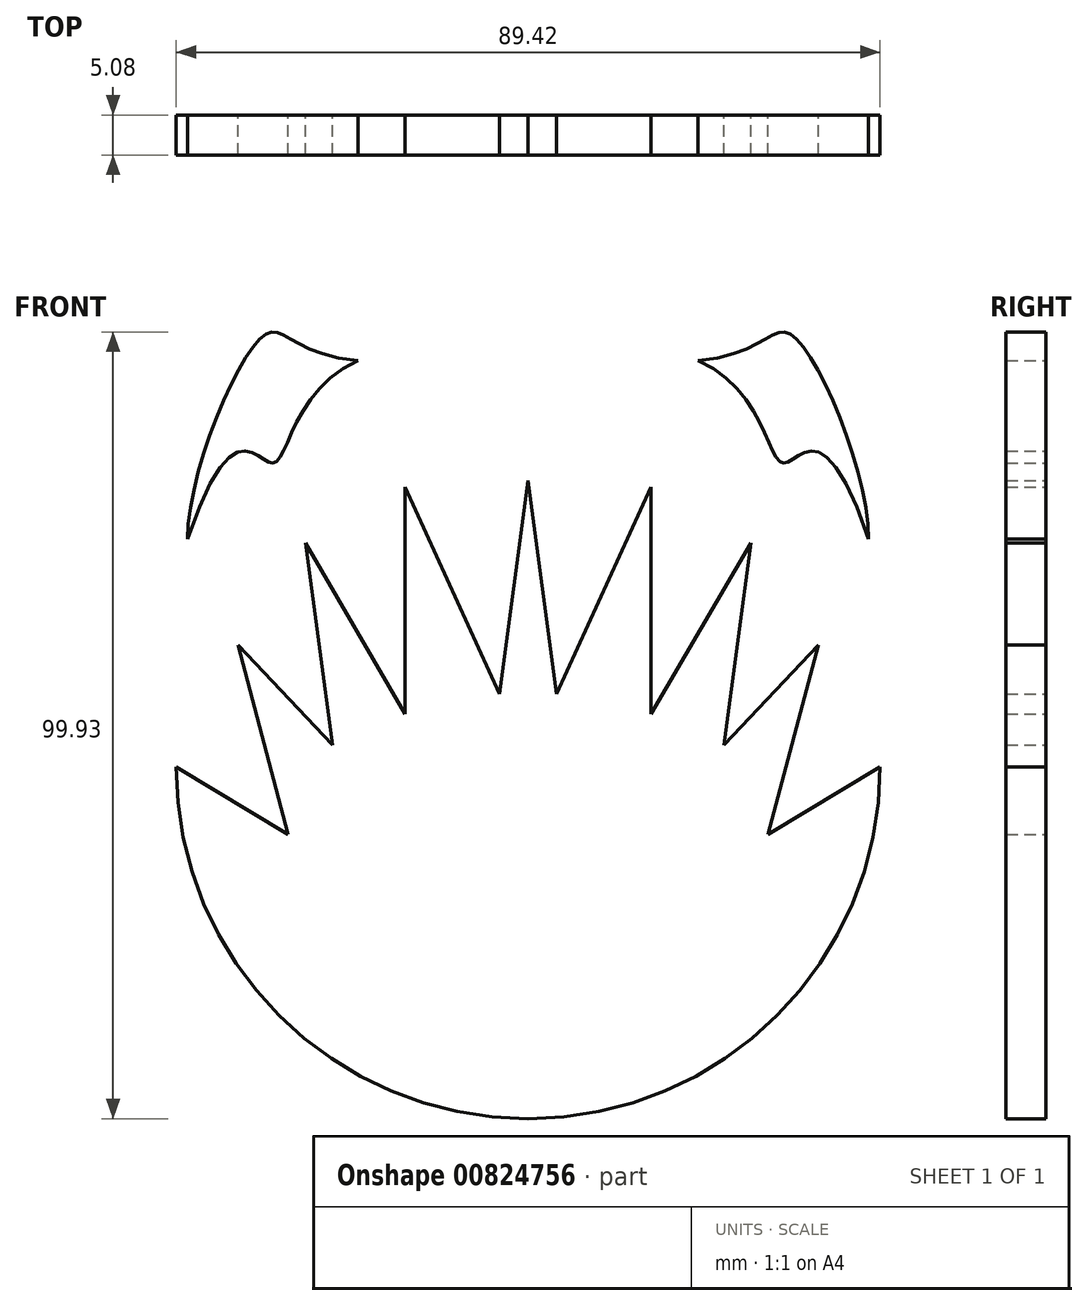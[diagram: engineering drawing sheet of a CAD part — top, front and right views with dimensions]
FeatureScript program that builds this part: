
annotation { "Feature Type Name" : "Feature", "Feature Type Description" : "" }
export const myFeature = defineFeature(function(context is Context, id is Id, definition is map)
    precondition{}
    {
        {
            var Q0;
            Q0=qCreatedBy(makeId("Front.planeOp"),FACE);
            var sketch = newSketch(context, id + "F0", { "sketchPlane" : qUnion([Q0])});
            skArc(sketch, "E0", {"start": v(-44.71, 0) * mm, "mid": v(0, -44.71) * mm, "end": v(44.71, 0) * mm});
            skLineSegment(sketch, "E1", {"start": v(0, 36.33) * mm, "end": v(3.6, 9.24) * mm});
            skLineSegment(sketch, "E2", {"start": v(3.6, 9.24) * mm, "end": v(15.63, 35.53) * mm});
            skLineSegment(sketch, "E3", {"start": v(15.63, 35.53) * mm, "end": v(15.63, 6.69) * mm});
            skLineSegment(sketch, "E4", {"start": v(15.63, 6.69) * mm, "end": v(28.3, 28.4) * mm});
            skLineSegment(sketch, "E5", {"start": v(28.3, 28.4) * mm, "end": v(24.87, 2.77) * mm});
            skLineSegment(sketch, "E6", {"start": v(24.87, 2.77) * mm, "end": v(36.87, 15.46) * mm});
            skLineSegment(sketch, "E7", {"start": v(36.87, 15.46) * mm, "end": v(30.5, -8.6) * mm});
            skLineSegment(sketch, "E8", {"start": v(30.5, -8.6) * mm, "end": v(44.71, 0) * mm});
            skLineSegment(sketch, "E9.MirrorCS", {"start": v(0, 36.33) * mm, "end": v(-3.6, 9.24) * mm});
            skLineSegment(sketch, "E10.MirrorCS", {"start": v(-3.6, 9.24) * mm, "end": v(-15.63, 35.53) * mm});
            skLineSegment(sketch, "E11.MirrorCS", {"start": v(-15.63, 35.53) * mm, "end": v(-15.63, 6.69) * mm});
            skLineSegment(sketch, "E12.MirrorCS", {"start": v(-15.63, 6.69) * mm, "end": v(-28.3, 28.4) * mm});
            skLineSegment(sketch, "E13.MirrorCS", {"start": v(-28.3, 28.4) * mm, "end": v(-24.87, 2.77) * mm});
            skLineSegment(sketch, "E14.MirrorCS", {"start": v(-24.87, 2.77) * mm, "end": v(-36.87, 15.46) * mm});
            skLineSegment(sketch, "E15.MirrorCS", {"start": v(-36.87, 15.46) * mm, "end": v(-30.5, -8.6) * mm});
            skLineSegment(sketch, "E16.MirrorCS", {"start": v(-30.5, -8.6) * mm, "end": v(-44.71, 0) * mm});
            skFitSpline(sketch, "E17", {"points": [v(-43.26, 28.91) * mm, v(-33.44, 54.85) * mm, v(-21.59, 51.57) * mm], "startDerivative": vector(0, 41.8) * mm, "endDerivative": vector(62.53, -5.77) * mm});
            skFitSpline(sketch, "E18", {"points": [v(-43.26, 28.91) * mm, v(-32.42, 38.58) * mm, v(-21.59, 51.57) * mm], "startDerivative": vector(35.65, 106.53) * mm, "endDerivative": vector(48.17, 20.56) * mm});
            skFitSpline(sketch, "E19.MirrorCS", {"points": [v(43.26, 28.91) * mm, v(32.42, 38.58) * mm, v(21.59, 51.57) * mm], "startDerivative": vector(-35.65, 106.53) * mm, "endDerivative": vector(-48.17, 20.56) * mm});
            skFitSpline(sketch, "E20.MirrorCS", {"points": [v(43.26, 28.91) * mm, v(33.44, 54.85) * mm, v(21.59, 51.57) * mm], "startDerivative": vector(0, 41.8) * mm, "endDerivative": vector(-62.53, -5.77) * mm});
            skPoint(sketch, "E21.MirrorCS.1.internal.orphan", {"position": v(0, 36.33) * mm});
            skSolve(sketch);
        }
        {
            var Q0;
            Q0 = qSketchRegion(id + "F0", true);
            extrude(context, id + "F1", {"entities" : qUnion([Q0]), "depth" : 5.08 * mm, "offsetDistance" : 25.4 * mm});
        }
    });
